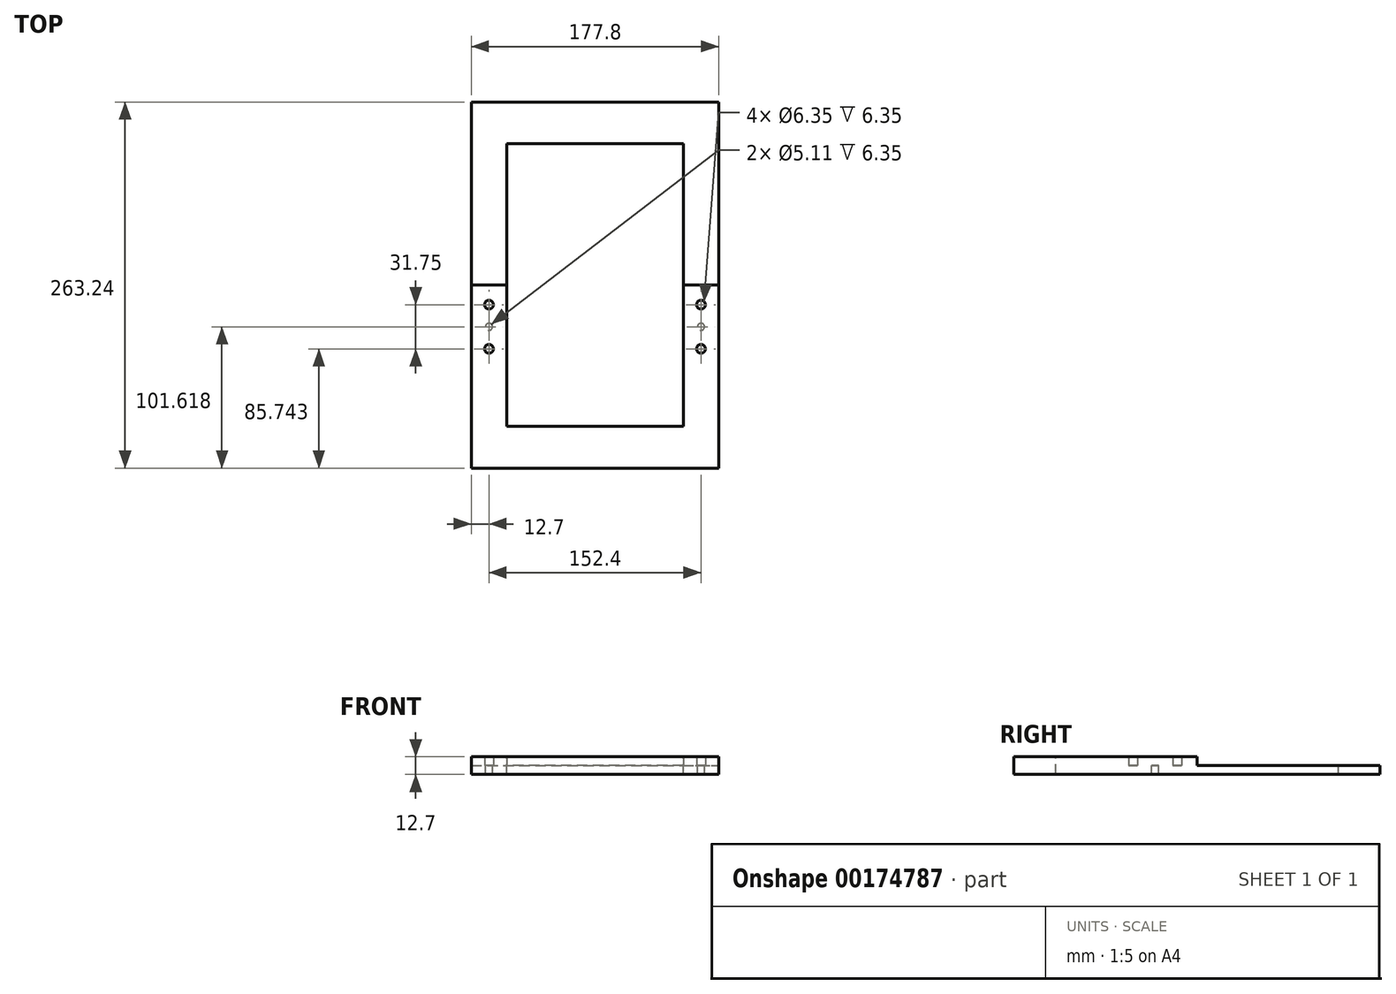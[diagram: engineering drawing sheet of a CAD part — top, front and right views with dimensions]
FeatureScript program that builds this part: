
annotation { "Feature Type Name" : "Feature", "Feature Type Description" : "" }
export const myFeature = defineFeature(function(context is Context, id is Id, definition is map)
    precondition{}
    {
        {
            var Q0;
            Q0=qCreatedBy(makeId("Top.planeOp"),FACE);
            var sketch = newSketch(context, id + "F0", { "sketchPlane" : qUnion([Q0])});
            skLineSegment(sketch, "E0.bottom", {"start": v(0, 0) * mm, "end": v(177.8, 0) * mm});
            skLineSegment(sketch, "E0.top", {"start": v(0, 263.24) * mm, "end": v(177.8, 263.24) * mm});
            skLineSegment(sketch, "E0.left", {"start": v(0, 0) * mm, "end": v(0, 263.24) * mm});
            skLineSegment(sketch, "E0.right", {"start": v(177.8, 0) * mm, "end": v(177.8, 263.24) * mm});
            skSolve(sketch);
        }
        {
            var Q0;
            Q0 = qSketchRegion(id + "F0", true);
            extrude(context, id + "F1", {"entities" : qUnion([Q0]), "depth" : 6.35 * mm});
        }
        {
            var Q0;
            Q0=makeQuery(id+"F1.opExtrude","CAP_FACE",FACE,{"disambiguationData":[OSD([sQuery(id+"F0.wireOp",EDGE,"E0.bottom"),sQuery(id+"F0.wireOp",EDGE,"E0.top"),sQuery(id+"F0.wireOp",EDGE,"E0.left"),sQuery(id+"F0.wireOp",EDGE,"E0.right")])],"isStart":false});
            var sketch = newSketch(context, id + "F2", { "sketchPlane" : qUnion([Q0])});
            skLineSegment(sketch, "E1", {"start": v(0, 131.62) * mm, "end": v(177.8, 131.62) * mm});
            skLineSegment(sketch, "E2", {"start": v(88.9, 263.24) * mm, "end": v(88.9, 0) * mm});
            skLineSegment(sketch, "E3.bottom", {"start": v(152.4, 233.22) * mm, "end": v(25.4, 233.22) * mm});
            skLineSegment(sketch, "E3.top", {"start": v(152.4, 30.02) * mm, "end": v(25.4, 30.02) * mm});
            skLineSegment(sketch, "E3.left", {"start": v(152.4, 233.22) * mm, "end": v(152.4, 30.02) * mm});
            skLineSegment(sketch, "E3.right", {"start": v(25.4, 233.22) * mm, "end": v(25.4, 30.02) * mm});
            skPoint(sketch, "E3.middle", {"position": v(88.9, 131.62) * mm});
            skSolve(sketch);
        }
        {
            var Q0;
            Q0 = qSketchRegion(id + "F2", true);
            extrude(context, id + "F3", {"entities" : qUnion([Q0]), "operationType" : NewBodyOperationType.REMOVE, "oppositeDirection" : true, "depth" : 25 * mm});
        }
        {
            var Q0;
            Q0=makeQuery(id+"F1.opExtrude","CAP_FACE",FACE,{"disambiguationData":[OSD([sQuery(id+"F0.wireOp",EDGE,"E0.bottom"),sQuery(id+"F0.wireOp",EDGE,"E0.top"),sQuery(id+"F0.wireOp",EDGE,"E0.left"),sQuery(id+"F0.wireOp",EDGE,"E0.right")])],"isStart":false});
            var sketch = newSketch(context, id + "F4", { "sketchPlane" : qUnion([Q0])});
            skLineSegment(sketch, "E4", {"start": v(12.7, 263.24) * mm, "end": v(12.7, 0) * mm});
            skLineSegment(sketch, "E5", {"start": v(165.1, 263.24) * mm, "end": v(165.1, 0) * mm});
            skLineSegment(sketch, "E6", {"start": v(88.9, 263.24) * mm, "end": v(88.9, 0) * mm});
            skLineSegment(sketch, "E7", {"start": v(0, 131.62) * mm, "end": v(177.8, 131.62) * mm});
            skLineSegment(sketch, "E8", {"start": v(177.8, 101.62) * mm, "end": v(0, 101.62) * mm});
            skPoint(sketch, "E9", {"position": v(12.7, 117.5) * mm});
            skPoint(sketch, "E10", {"position": v(12.7, 85.74) * mm});
            skPoint(sketch, "E11", {"position": v(165.1, 117.5) * mm});
            skPoint(sketch, "E12", {"position": v(165.1, 85.74) * mm});
            skCircle(sketch, "E13", {"center": v(12.7, 117.5) * mm, "radius": 3.18 * mm});
            skCircle(sketch, "E14", {"center": v(12.7, 85.74) * mm, "radius": 3.18 * mm});
            skCircle(sketch, "E15", {"center": v(165.1, 117.5) * mm, "radius": 3.18 * mm});
            skCircle(sketch, "E16", {"center": v(165.1, 85.74) * mm, "radius": 3.18 * mm});
            skPoint(sketch, "E17", {"position": v(12.7, 101.62) * mm});
            skPoint(sketch, "E18", {"position": v(165.1, 101.62) * mm});
            skSolve(sketch);
        }
        {
            var Q0;
            Q0=sQuery(id+"F4.wireOp",VERTEX,"E17");
            var Q1;
            Q1=sQuery(id+"F4.wireOp",VERTEX,"E18");
            var Q2;
            Q2=makeQuery(id+"F1.opExtrude","SWEPT_BODY",BODY,{"disambiguationData":[OSD([sQuery(id+"F0.wireOp",EDGE,"E0.bottom"),sQuery(id+"F0.wireOp",EDGE,"E0.top"),sQuery(id+"F0.wireOp",EDGE,"E0.left"),sQuery(id+"F0.wireOp",EDGE,"E0.right")])]});
            hole(context, id + "F5", {"style" : HoleStyle.SIMPLE, "endStyle" : HoleEndStyle.THROUGH, "standardTappedOrClearance" : lookupTablePath({ "standard" : "ANSI", "engagement" : "75%", "pitch" : "20 tpi", "size" : "1/4", "type" : "Tapped" }), "standardBlindInLast" : lookupTablePath({ "standard" : "ANSI", "engagement" : "75%", "pitch" : "20 tpi", "size" : "1/4", "type" : "Tapped" }), "holeDiameter" : 5.1 * mm, "locations" : qUnion([Q0, Q1]), "scope" : qUnion([Q2]), "isTappedThrough" : true, "majorDiameter" : 6.35 * mm, "showTappedDepth" : true});
        }
        {
            var Q0;
            {var subQ0=sQuery(id+"F4.wireOp",EDGE,"E15");var subQ1=sQuery(id+"F4.wireOp",EDGE,"E5");var subQ2=makeQuery(id+"F4.imprint","INTERSECT",VERTEX,{"disambiguationData":[OD(0.0)],"derivedFrom":[subQ1,subQ0]});Q0=makeQuery(id+"F4.imprint","IMPRINT",FACE,{"disambiguationData":[TD([[makeQuery(id+"F4.imprint","IMPRINT",EDGE,{"disambiguationData":[TD([[subQ2,-1.0]])],"derivedFrom":subQ1}),1.0]])]});}
            var Q1;
            {var subQ0=sQuery(id+"F4.wireOp",EDGE,"E15");var subQ1=sQuery(id+"F4.wireOp",EDGE,"E5");var subQ2=makeQuery(id+"F4.imprint","INTERSECT",VERTEX,{"disambiguationData":[OD(0.0)],"derivedFrom":[subQ1,subQ0]});Q1=makeQuery(id+"F4.imprint","IMPRINT",FACE,{"disambiguationData":[TD([[makeQuery(id+"F4.imprint","IMPRINT",EDGE,{"disambiguationData":[TD([[subQ2,-1.0]])],"derivedFrom":subQ1}),-1.0]])]});}
            var Q2;
            {var subQ0=sQuery(id+"F4.wireOp",EDGE,"E16");var subQ1=sQuery(id+"F4.wireOp",EDGE,"E5");var subQ2=makeQuery(id+"F4.imprint","INTERSECT",VERTEX,{"disambiguationData":[OD(0.0)],"derivedFrom":[subQ1,subQ0]});Q2=makeQuery(id+"F4.imprint","IMPRINT",FACE,{"disambiguationData":[TD([[makeQuery(id+"F4.imprint","IMPRINT",EDGE,{"disambiguationData":[TD([[subQ2,-1.0]])],"derivedFrom":subQ1}),1.0]])]});}
            var Q3;
            {var subQ0=sQuery(id+"F4.wireOp",EDGE,"E16");var subQ1=sQuery(id+"F4.wireOp",EDGE,"E5");var subQ2=makeQuery(id+"F4.imprint","INTERSECT",VERTEX,{"disambiguationData":[OD(0.0)],"derivedFrom":[subQ1,subQ0]});Q3=makeQuery(id+"F4.imprint","IMPRINT",FACE,{"disambiguationData":[TD([[makeQuery(id+"F4.imprint","IMPRINT",EDGE,{"disambiguationData":[TD([[subQ2,-1.0]])],"derivedFrom":subQ1}),-1.0]])]});}
            var Q4;
            {var subQ0=sQuery(id+"F4.wireOp",EDGE,"E14");var subQ1=sQuery(id+"F4.wireOp",EDGE,"E4");var subQ2=makeQuery(id+"F4.imprint","INTERSECT",VERTEX,{"disambiguationData":[OD(0.0)],"derivedFrom":[subQ1,subQ0]});Q4=makeQuery(id+"F4.imprint","IMPRINT",FACE,{"disambiguationData":[TD([[makeQuery(id+"F4.imprint","IMPRINT",EDGE,{"disambiguationData":[TD([[subQ2,-1.0]])],"derivedFrom":subQ1}),1.0]])]});}
            var Q5;
            {var subQ0=sQuery(id+"F4.wireOp",EDGE,"E14");var subQ1=sQuery(id+"F4.wireOp",EDGE,"E4");var subQ2=makeQuery(id+"F4.imprint","INTERSECT",VERTEX,{"disambiguationData":[OD(0.0)],"derivedFrom":[subQ1,subQ0]});Q5=makeQuery(id+"F4.imprint","IMPRINT",FACE,{"disambiguationData":[TD([[makeQuery(id+"F4.imprint","IMPRINT",EDGE,{"disambiguationData":[TD([[subQ2,-1.0]])],"derivedFrom":subQ1}),-1.0]])]});}
            var Q6;
            {var subQ0=sQuery(id+"F4.wireOp",EDGE,"E13");var subQ1=sQuery(id+"F4.wireOp",EDGE,"E4");var subQ2=makeQuery(id+"F4.imprint","INTERSECT",VERTEX,{"disambiguationData":[OD(0.0)],"derivedFrom":[subQ1,subQ0]});Q6=makeQuery(id+"F4.imprint","IMPRINT",FACE,{"disambiguationData":[TD([[makeQuery(id+"F4.imprint","IMPRINT",EDGE,{"disambiguationData":[TD([[subQ2,-1.0]])],"derivedFrom":subQ1}),1.0]])]});}
            var Q7;
            {var subQ0=sQuery(id+"F4.wireOp",EDGE,"E13");var subQ1=sQuery(id+"F4.wireOp",EDGE,"E4");var subQ2=makeQuery(id+"F4.imprint","INTERSECT",VERTEX,{"disambiguationData":[OD(0.0)],"derivedFrom":[subQ1,subQ0]});Q7=makeQuery(id+"F4.imprint","IMPRINT",FACE,{"disambiguationData":[TD([[makeQuery(id+"F4.imprint","IMPRINT",EDGE,{"disambiguationData":[TD([[subQ2,-1.0]])],"derivedFrom":subQ1}),-1.0]])]});}
            extrude(context, id + "F6", {"entities" : qUnion([Q0, Q1, Q2, Q3, Q4, Q5, Q6, Q7]), "operationType" : NewBodyOperationType.ADD, "depth" : 6.35 * mm});
        }
    });
